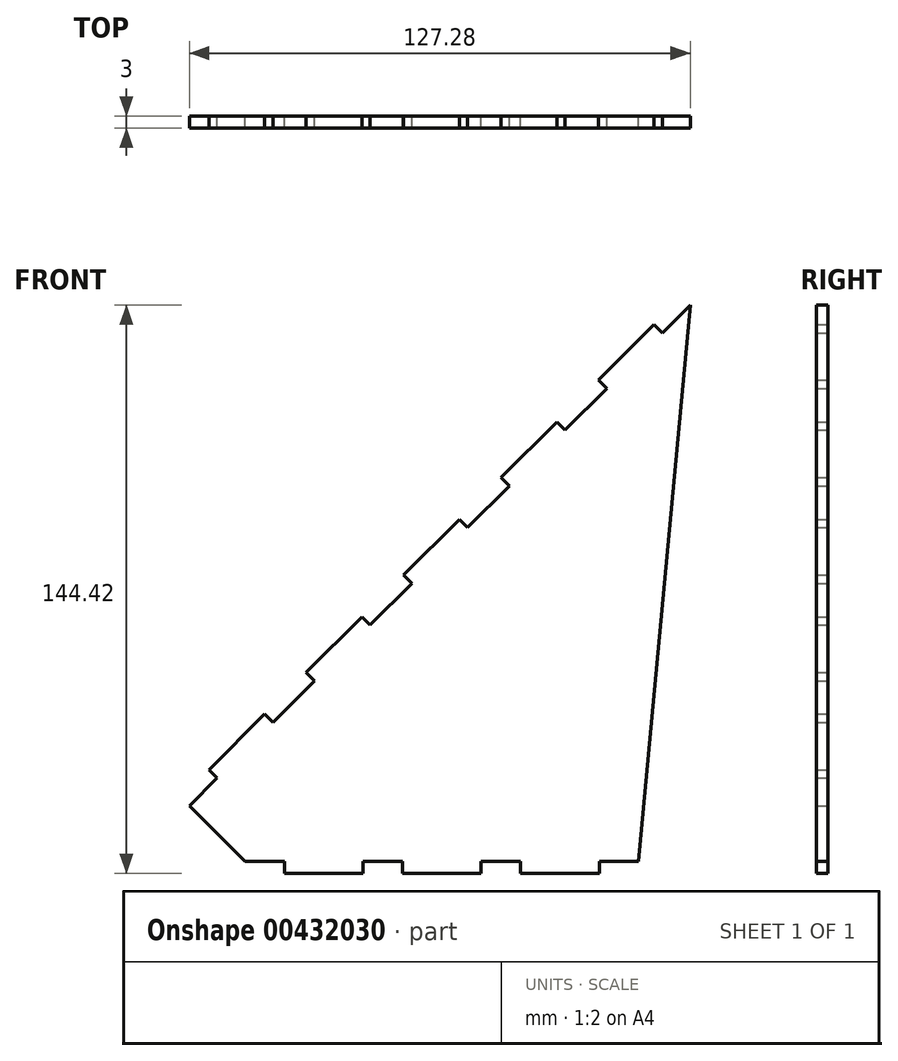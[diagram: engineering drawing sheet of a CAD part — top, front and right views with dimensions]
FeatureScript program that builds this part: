
annotation { "Feature Type Name" : "Feature", "Feature Type Description" : "" }
export const myFeature = defineFeature(function(context is Context, id is Id, definition is map)
    precondition{}
    {
        {
            var Q0;
            Q0=qCreatedBy(makeId("Front.planeOp"),FACE);
            var sketch = newSketch(context, id + "F0", { "sketchPlane" : qUnion([Q0])});
            skLineSegment(sketch, "E0", {"start": v(0, 75.75) * mm, "end": v(-7.07, 68.68) * mm});
            skLineSegment(sketch, "E1", {"start": v(-127.28, -51.53) * mm, "end": v(-113.14, -65.67) * mm});
            skLineSegment(sketch, "E2", {"start": v(-113.14, -65.67) * mm, "end": v(-103.14, -65.67) * mm});
            skLineSegment(sketch, "E3", {"start": v(-13.14, -65.67) * mm, "end": v(0, 75.75) * mm});
            skLineSegment(sketch, "E4", {"start": v(-65.76, 14.23) * mm, "end": v(-58.69, 21.3) * mm});
            skLineSegment(sketch, "E5", {"start": v(-58.69, 21.3) * mm, "end": v(-56.57, 19.18) * mm});
            skLineSegment(sketch, "E6", {"start": v(-65.76, 14.23) * mm, "end": v(-72.83, 7.16) * mm});
            skLineSegment(sketch, "E7", {"start": v(-72.83, 7.16) * mm, "end": v(-70.71, 5.04) * mm});
            skLineSegment(sketch, "E8.trimOffspring", {"start": v(-70.71, 5.04) * mm, "end": v(-81.32, -5.57) * mm});
            skPoint(sketch, "E9.start.orphan", {"position": v(-63.64, 12.11) * mm});
            skLineSegment(sketch, "E10", {"start": v(-81.32, -5.57) * mm, "end": v(-83.44, -3.45) * mm});
            skLineSegment(sketch, "E11", {"start": v(-83.44, -3.45) * mm, "end": v(-97.58, -17.59) * mm});
            skLineSegment(sketch, "E12", {"start": v(-97.58, -17.59) * mm, "end": v(-95.46, -19.7) * mm});
            skLineSegment(sketch, "E13.trimOffspring", {"start": v(-95.46, -19.7) * mm, "end": v(-106.07, -30.32) * mm});
            skLineSegment(sketch, "E14", {"start": v(-106.07, -30.32) * mm, "end": v(-108.19, -28.2) * mm});
            skLineSegment(sketch, "E15", {"start": v(-108.19, -28.2) * mm, "end": v(-122.33, -42.34) * mm});
            skLineSegment(sketch, "E16", {"start": v(-122.33, -42.34) * mm, "end": v(-120.2, -44.46) * mm});
            skLineSegment(sketch, "E17.trimOffspring", {"start": v(-120.2, -44.46) * mm, "end": v(-127.28, -51.53) * mm});
            skLineSegment(sketch, "E18", {"start": v(-45.96, 29.79) * mm, "end": v(-48.08, 31.9) * mm});
            skLineSegment(sketch, "E19", {"start": v(-48.08, 31.9) * mm, "end": v(-33.94, 46.05) * mm});
            skLineSegment(sketch, "E20", {"start": v(-33.94, 46.05) * mm, "end": v(-31.82, 43.93) * mm});
            skLineSegment(sketch, "E21.trimOffspring", {"start": v(-45.96, 29.79) * mm, "end": v(-56.57, 19.18) * mm});
            skLineSegment(sketch, "E22", {"start": v(-21.21, 54.54) * mm, "end": v(-23.33, 56.66) * mm});
            skLineSegment(sketch, "E23", {"start": v(-23.33, 56.66) * mm, "end": v(-9.2, 70.8) * mm});
            skLineSegment(sketch, "E24", {"start": v(-9.2, 70.8) * mm, "end": v(-7.07, 68.68) * mm});
            skLineSegment(sketch, "E25.trimOffspring", {"start": v(-21.21, 54.54) * mm, "end": v(-31.82, 43.93) * mm});
            skLineSegment(sketch, "E26", {"start": v(-73.14, -65.67) * mm, "end": v(-73.14, -68.67) * mm});
            skLineSegment(sketch, "E27", {"start": v(-73.14, -68.67) * mm, "end": v(-53.14, -68.67) * mm});
            skLineSegment(sketch, "E28", {"start": v(-53.14, -68.67) * mm, "end": v(-53.14, -65.67) * mm});
            skLineSegment(sketch, "E29.trimOffspring", {"start": v(-53.14, -65.67) * mm, "end": v(-43.14, -65.67) * mm});
            skLineSegment(sketch, "E30", {"start": v(-43.14, -65.67) * mm, "end": v(-43.14, -68.67) * mm});
            skLineSegment(sketch, "E31", {"start": v(-43.14, -68.67) * mm, "end": v(-23.14, -68.67) * mm});
            skLineSegment(sketch, "E32", {"start": v(-23.14, -68.67) * mm, "end": v(-23.14, -65.67) * mm});
            skLineSegment(sketch, "E33.trimOffspring", {"start": v(-23.14, -65.67) * mm, "end": v(-13.14, -65.67) * mm});
            skLineSegment(sketch, "E34", {"start": v(-83.14, -65.67) * mm, "end": v(-83.14, -68.67) * mm});
            skLineSegment(sketch, "E35", {"start": v(-83.14, -68.67) * mm, "end": v(-103.14, -68.67) * mm});
            skLineSegment(sketch, "E36", {"start": v(-103.14, -68.67) * mm, "end": v(-103.14, -65.67) * mm});
            skLineSegment(sketch, "E37.trimOffspring", {"start": v(-83.14, -65.67) * mm, "end": v(-73.14, -65.67) * mm});
            skSolve(sketch);
        }
        {
            var Q0;
            Q0=makeQuery(id+"F0.imprint","IMPRINT",FACE,{"disambiguationData":[TD([[makeQuery(id+"F0.imprint","IMPRINT",EDGE,{"derivedFrom":sQuery(id+"F0.wireOp",EDGE,"E0")}),1.0]])]});
            extrude(context, id + "F1", {"entities" : qUnion([Q0]), "depth" : 3 * mm});
        }
    });
